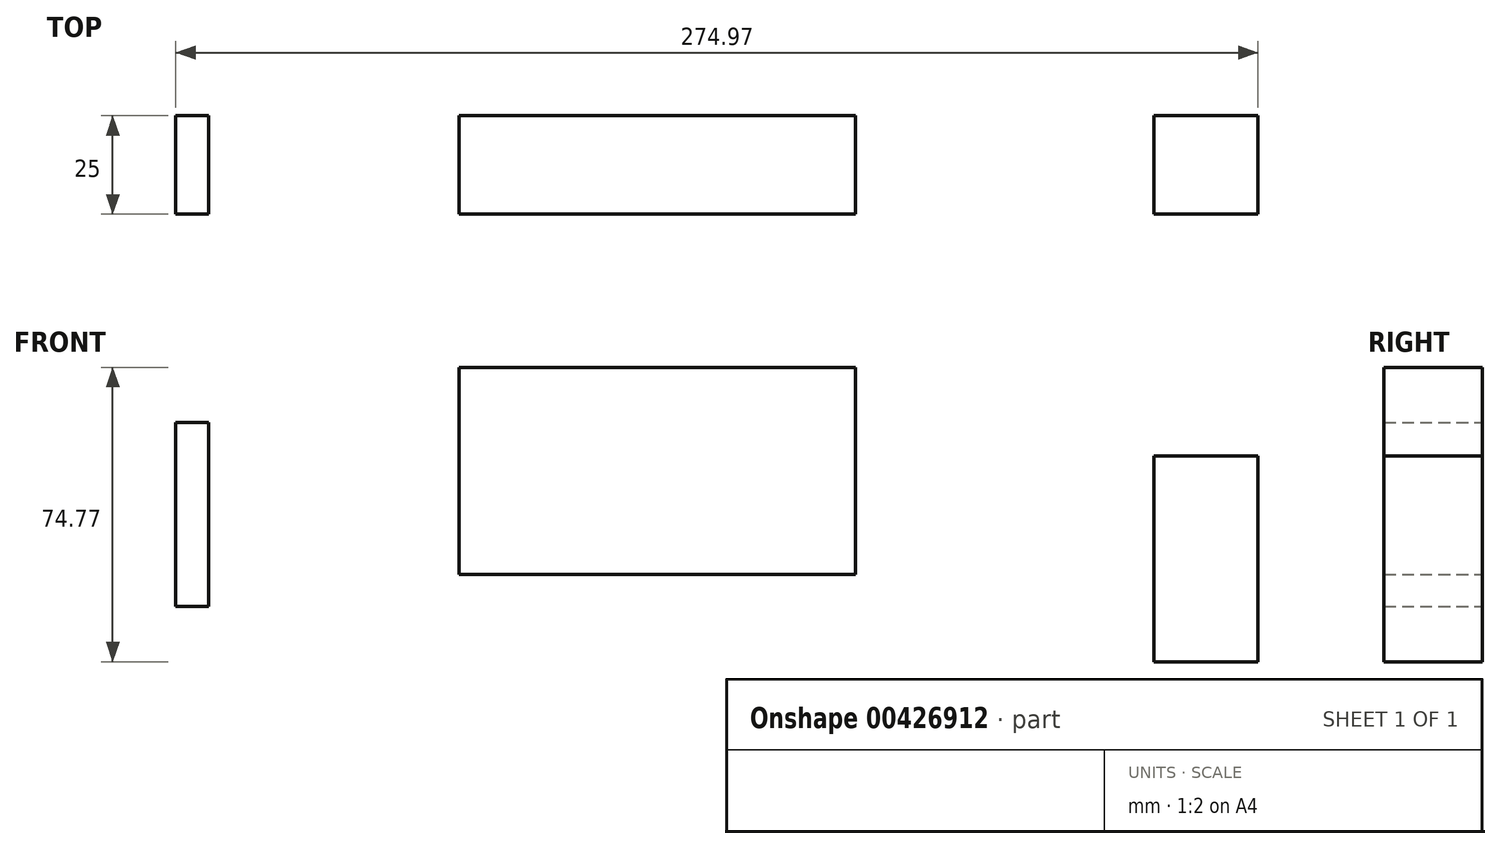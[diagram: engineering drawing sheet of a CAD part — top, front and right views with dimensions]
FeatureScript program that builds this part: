
annotation { "Feature Type Name" : "Feature", "Feature Type Description" : "" }
export const myFeature = defineFeature(function(context is Context, id is Id, definition is map)
    precondition{}
    {
        {
            var Q0;
            Q0=qCreatedBy(makeId("Front.planeOp"),FACE);
            var sketch = newSketch(context, id + "F0", { "sketchPlane" : qUnion([Q0])});
            skLineSegment(sketch, "E0.bottom", {"start": v(-132.4, 43.8) * mm, "end": v(-124.1, 43.8) * mm});
            skLineSegment(sketch, "E0.top", {"start": v(-132.4, -3) * mm, "end": v(-124.1, -3) * mm});
            skLineSegment(sketch, "E0.left", {"start": v(-132.4, 43.8) * mm, "end": v(-132.4, -3) * mm});
            skLineSegment(sketch, "E0.right", {"start": v(-124.1, 43.8) * mm, "end": v(-124.1, -3) * mm});
            skLineSegment(sketch, "E1.bottom", {"start": v(-60.4, 57.7) * mm, "end": v(40.22, 57.7) * mm});
            skLineSegment(sketch, "E1.top", {"start": v(-60.4, 5.08) * mm, "end": v(40.22, 5.08) * mm});
            skLineSegment(sketch, "E1.left", {"start": v(-60.4, 57.7) * mm, "end": v(-60.4, 5.08) * mm});
            skLineSegment(sketch, "E1.right", {"start": v(40.22, 57.7) * mm, "end": v(40.22, 5.08) * mm});
            skLineSegment(sketch, "E2.bottom", {"start": v(116.03, 35.23) * mm, "end": v(142.56, 35.23) * mm});
            skLineSegment(sketch, "E2.top", {"start": v(116.03, -17.07) * mm, "end": v(142.56, -17.07) * mm});
            skLineSegment(sketch, "E2.left", {"start": v(116.03, 35.23) * mm, "end": v(116.03, -17.07) * mm});
            skLineSegment(sketch, "E2.right", {"start": v(142.56, 35.23) * mm, "end": v(142.56, -17.07) * mm});
            skSolve(sketch);
        }
        {
            var Q0;
            Q0=makeQuery(id+"F0.imprint","IMPRINT",FACE,{"disambiguationData":[TD([[makeQuery(id+"F0.imprint","IMPRINT",EDGE,{"derivedFrom":sQuery(id+"F0.wireOp",EDGE,"E0.bottom")}),-1.0]])]});
            var Q1;
            Q1=makeQuery(id+"F0.imprint","IMPRINT",FACE,{"disambiguationData":[TD([[makeQuery(id+"F0.imprint","IMPRINT",EDGE,{"derivedFrom":sQuery(id+"F0.wireOp",EDGE,"E1.bottom")}),-1.0]])]});
            var Q2;
            Q2=makeQuery(id+"F0.imprint","IMPRINT",FACE,{"disambiguationData":[TD([[makeQuery(id+"F0.imprint","IMPRINT",EDGE,{"derivedFrom":sQuery(id+"F0.wireOp",EDGE,"E2.bottom")}),-1.0]])]});
            extrude(context, id + "F1", {"entities" : qUnion([Q0, Q1, Q2]), "depth" : 25 * mm});
        }
    });
